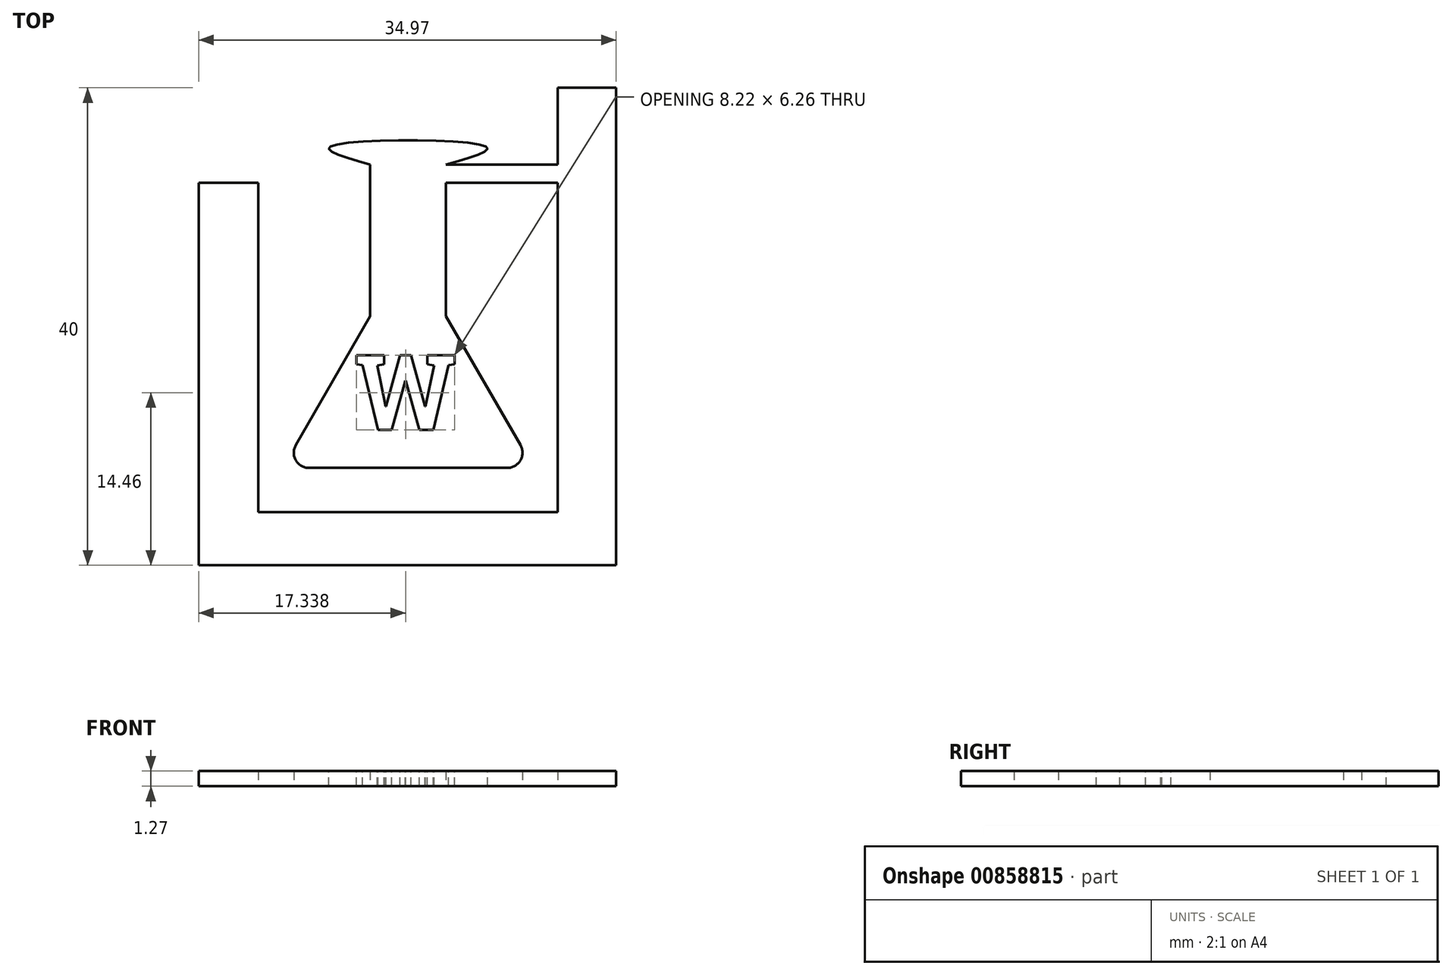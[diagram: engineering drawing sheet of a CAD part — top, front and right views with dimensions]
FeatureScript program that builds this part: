
annotation { "Feature Type Name" : "Feature", "Feature Type Description" : "" }
export const myFeature = defineFeature(function(context is Context, id is Id, definition is map)
    precondition{}
    {
        {
            var Q0;
            Q0=qCreatedBy(makeId("Top.planeOp"),FACE);
            var sketch = newSketch(context, id + "F0", { "sketchPlane" : qUnion([Q0])});
            skLineSegment(sketch, "E0.top", {"start": v(17.42, -24.66) * mm, "end": v(-17.55, -24.66) * mm});
            skLineSegment(sketch, "E0.left", {"start": v(17.42, 15.34) * mm, "end": v(17.42, -24.66) * mm});
            skLineSegment(sketch, "E0.right", {"start": v(-17.55, -0.21) * mm, "end": v(-17.55, -24.66) * mm});
            skLineSegment(sketch, "E1.top", {"start": v(12.52, -20.21) * mm, "end": v(-12.55, -20.21) * mm});
            skLineSegment(sketch, "E1.right", {"start": v(-12.55, -0.21) * mm, "end": v(-12.55, -20.21) * mm});
            skLineSegment(sketch, "E2.trimOffspring", {"start": v(12.52, 3.19) * mm, "end": v(12.52, -20.21) * mm});
            skPoint(sketch, "E3.MirrorCS.end.orphan", {"position": v(17.5, 16.1) * mm});
            skPoint(sketch, "E3.MirrorCS.start.orphan", {"position": v(12.5, 15.55) * mm});
            skLineSegment(sketch, "E4", {"start": v(12.52, 15.34) * mm, "end": v(17.42, 15.34) * mm});
            skPoint(sketch, "E5.MirrorCS.start.orphan", {"position": v(17.5, 15.55) * mm});
            skLineSegment(sketch, "E6", {"start": v(12.52, 15.34) * mm, "end": v(12.52, 10.97) * mm});
            skLineSegment(sketch, "E7.trimOffspring", {"start": v(12.52, 7.37) * mm, "end": v(12.52, 3.19) * mm});
            skLineSegment(sketch, "E8", {"start": v(12.52, 10.97) * mm, "end": v(12.52, 8.9) * mm});
            skLineSegment(sketch, "E9.left", {"start": v(3.18, 7.37) * mm, "end": v(3.18, -3.8) * mm});
            skLineSegment(sketch, "E9.right", {"start": v(-3.18, 8.89) * mm, "end": v(-3.18, -3.8) * mm});
            skPoint(sketch, "E9.middle", {"position": v(0, 2.54) * mm});
            skLineSegment(sketch, "E10", {"start": v(-3.18, -3.8) * mm, "end": v(-9.4, -14.6) * mm});
            skLineSegment(sketch, "E11.MirrorCS", {"start": v(3.17, -3.8) * mm, "end": v(9.4, -14.6) * mm});
            skLineSegment(sketch, "E12", {"start": v(-8.3, -16.51) * mm, "end": v(8.3, -16.5) * mm});
            skPoint(sketch, "E13.visualSharp", {"position": v(10.5, -16.51) * mm});
            skArc(sketch, "E13.filletArc", {"start": v(8.3, -16.5) * mm, "mid": v(9.4, -15.88) * mm, "end": v(9.4, -14.6) * mm});
            skPoint(sketch, "E14.visualSharp", {"position": v(-10.5, -16.51) * mm});
            skArc(sketch, "E14.filletArc", {"start": v(-9.4, -14.6) * mm, "mid": v(-9.4, -15.88) * mm, "end": v(-8.3, -16.5) * mm});
            skPoint(sketch, "E15.start.orphan", {"position": v(-2.32, 0) * mm});
            skFitSpline(sketch, "E16", {"points": [v(-3.18, 8.9) * mm, v(-6.53, 10.41) * mm, v(6.53, 10.41) * mm, v(3.18, 8.9) * mm], "startDerivative": vector(-23.3, 6.7) * mm, "endDerivative": vector(-23.3, -6.7) * mm});
            skLineSegment(sketch, "E17", {"start": v(3.17, 7.37) * mm, "end": v(12.52, 7.37) * mm});
            skLineSegment(sketch, "E18", {"start": v(3.18, 8.9) * mm, "end": v(12.52, 8.9) * mm});
            skLineSegment(sketch, "E19.left", {"start": v(-17.55, -0.21) * mm, "end": v(-17.55, 7.37) * mm});
            skLineSegment(sketch, "E20.trimOffspring", {"start": v(-13.65, 7.37) * mm, "end": v(-17.64, 7.37) * mm});
            skLineSegment(sketch, "E21.top", {"start": v(-12.55, 7.37) * mm, "end": v(-13.65, 7.37) * mm});
            skLineSegment(sketch, "E21.left", {"start": v(-12.55, -0.21) * mm, "end": v(-12.55, 7.37) * mm});
            skLineSegment(sketch, "E22", {"start": v(0, -16.51) * mm, "end": v(0, -3.8) * mm, "construction": true});
            skPoint(sketch, "E23", {"position": v(0, -10.16) * mm});
            skSolve(sketch);
        }
        {
            var Q0;
            Q0=makeQuery(id+"F0.imprint","IMPRINT",FACE,{"disambiguationData":[TD([[makeQuery(id+"F0.imprint","IMPRINT",EDGE,{"derivedFrom":sQuery(id+"F0.wireOp",EDGE,"E0.top")}),-1.0]])]});
            var Q1;
            {var subQ0=sQuery(id+"F0.wireOp",EDGE,"FKejiANf-u82S-7BPr-4an4-q4Ka4m4IZFMA");var subQ1=makeQuery(id+"F0.imprint","INTERSECT",VERTEX,{"derivedFrom":[sQuery(id+"F0.wireOp",EDGE,"1SfU6YIB-wvzm-6zBe-5eDS-HKFIA9QaUayn"),subQ0]});Q1=makeQuery(id+"F0.imprint","IMPRINT",FACE,{"disambiguationData":[TD([[makeQuery(id+"F0.imprint","IMPRINT",EDGE,{"disambiguationData":[TD([[subQ1,1.0]])],"derivedFrom":subQ0}),1.0]])]});}
            extrude(context, id + "F1", {"entities" : qUnion([Q0, Q1]), "depth" : 1.27 * mm, "offsetDistance" : 25.4 * mm});
        }
        {
            var Q0;
            Q0=makeQuery(id+"F1.opExtrude","CAP_FACE",FACE,{"disambiguationData":[OSD([sQuery(id+"F0.wireOp",EDGE,"E0.top"),sQuery(id+"F0.wireOp",EDGE,"E0.left"),sQuery(id+"F0.wireOp",EDGE,"E0.right"),sQuery(id+"F0.wireOp",EDGE,"E1.top"),sQuery(id+"F0.wireOp",EDGE,"E1.right"),sQuery(id+"F0.wireOp",EDGE,"1SfU6YIB-wvzm-6zBe-5eDS-HKFIA9QaUayn"),sQuery(id+"F0.wireOp",EDGE,"sM1Sgktc-x2VY-oS3Z-5OfG-QNgHwikTJDgL"),sQuery(id+"F0.wireOp",EDGE,"7EqO3XEm-McEN-PWzp-HPdO-5mDO97qVc4eW"),sQuery(id+"F0.wireOp",EDGE,"BdKeHqo0-FdcT-Rb85-6iZA-lVtgPkFKthWV"),sQuery(id+"F0.wireOp",EDGE,"FKejiANf-u82S-7BPr-4an4-q4Ka4m4IZFMA"),sQuery(id+"F0.wireOp",EDGE,"eK1Uujpq-Df3w-NQqX-Gc2k-lf4LO3mh3muX"),sQuery(id+"F0.wireOp",EDGE,"9dokPukG-NNzw-ETl1-5EZM-OfzmBowc8QZ2"),sQuery(id+"F0.wireOp",EDGE,"89ef536c-63d7-428c-8d95-022694007808.trimOffspring"),sQuery(id+"F0.wireOp",EDGE,"e37d3fe4-c149-4dc4-956f-d1983d31f44f.trimOffspring"),sQuery(id+"F0.wireOp",EDGE,"E2.trimOffspring"),sQuery(id+"F0.wireOp",EDGE,"eCGh251j-4Mt1-Y2Ib-rAlh-B7rz0UIJvHUj"),sQuery(id+"F0.wireOp",EDGE,"E4")])],"isStart":false});
            var sketch = newSketch(context, id + "F2", { "sketchPlane" : qUnion([Q0])});
            skText(sketch, "E24", { "text": "W", "fontName": "RobotoSlab-Bold.ttf"});
            skPoint(sketch, "E25", {"position": v(0, -10.16) * mm});
            const initialGuessF2  = {"E24": [-0.00445, -0.01333, 1, 0, 0.00634]};
            skSetInitialGuess(sketch, initialGuessF2);
            skSolve(sketch);
        }
        {
            var Q0;
            Q0=makeQuery(id+"F2.imprint","IMPRINT",FACE,{"disambiguationData":[TD([[makeQuery(id+"F2.imprint","IMPRINT",EDGE,{"derivedFrom":sQuery(id+"F2.wireOp",EDGE,"E24.sketch_text.stroke-16")}),-1.0]])]});
            var Q1;
            Q1=makeQuery(id+"F2.imprint","IMPRINT",FACE,{"disambiguationData":[TD([[makeQuery(id+"F2.imprint","IMPRINT",EDGE,{"derivedFrom":sQuery(id+"F2.wireOp",EDGE,"E24.sketch_text.stroke-0")}),-1.0]])]});
            extrude(context, id + "F3", {"entities" : qUnion([Q0, Q1]), "operationType" : NewBodyOperationType.REMOVE, "oppositeDirection" : true, "depth" : 25.4 * mm, "offsetDistance" : 25.4 * mm});
        }
    });
